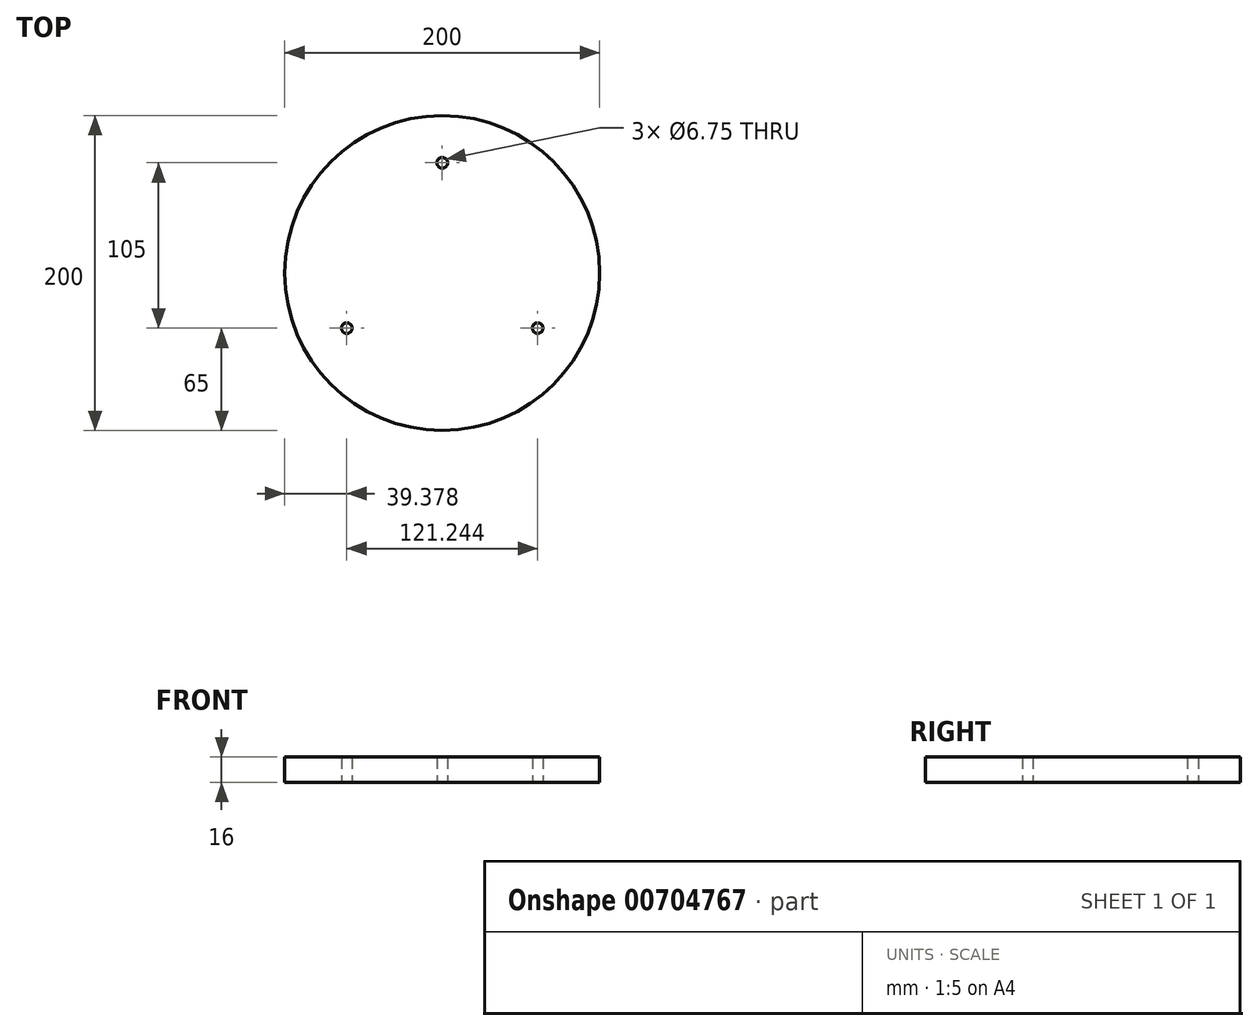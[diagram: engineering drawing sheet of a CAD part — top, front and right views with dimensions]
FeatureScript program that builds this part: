
annotation { "Feature Type Name" : "Feature", "Feature Type Description" : "" }
export const myFeature = defineFeature(function(context is Context, id is Id, definition is map)
    precondition{}
    {
        {
            var Q0;
            Q0=qCreatedBy(makeId("Top.planeOp"),FACE);
            var sketch = newSketch(context, id + "F0", { "sketchPlane" : qUnion([Q0])});
            skCircle(sketch, "E0", {"center": v(0, 0) * mm, "radius": 100 * mm});
            skCircle(sketch, "E1", {"center": v(0, 0) * mm, "radius": 70 * mm, "construction": true});
            skCircle(sketch, "E2", {"center": v(0, 70) * mm, "radius": 3.38 * mm});
            skLineSegment(sketch, "E3", {"start": v(0, 70) * mm, "end": v(-60.62, -35) * mm, "construction": true});
            skLineSegment(sketch, "E4", {"start": v(-60.62, -35) * mm, "end": v(60.62, -35) * mm, "construction": true});
            skLineSegment(sketch, "E5", {"start": v(0, 70) * mm, "end": v(60.62, -35) * mm, "construction": true});
            skCircle(sketch, "E6", {"center": v(-60.62, -35) * mm, "radius": 3.37 * mm});
            skCircle(sketch, "E7", {"center": v(60.62, -35) * mm, "radius": 3.38 * mm});
            skSolve(sketch);
        }
        {
            var Q0;
            Q0=makeQuery(id+"F0.imprint","IMPRINT",FACE,{"disambiguationData":[TD([[makeQuery(id+"F0.imprint","IMPRINT",EDGE,{"derivedFrom":sQuery(id+"F0.wireOp",EDGE,"E0")}),1.0]])]});
            extrude(context, id + "F1", {"entities" : qUnion([Q0]), "depth" : 16 * mm, "offsetDistance" : 25 * mm});
        }
    });
